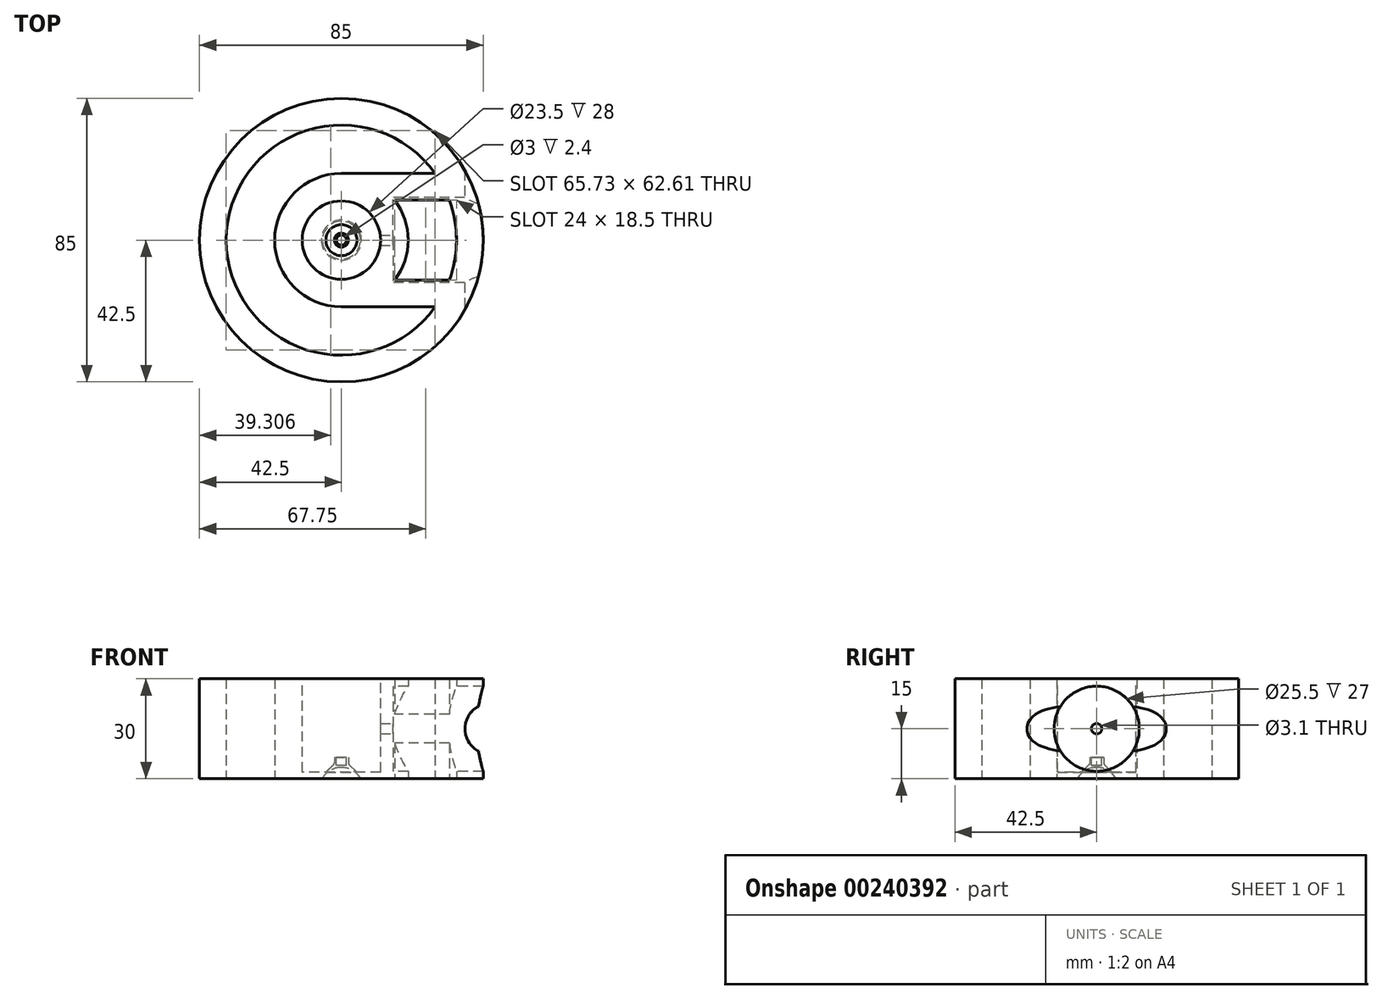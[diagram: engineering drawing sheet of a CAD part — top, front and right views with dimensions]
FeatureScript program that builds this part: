
annotation { "Feature Type Name" : "Feature", "Feature Type Description" : "" }
export const myFeature = defineFeature(function(context is Context, id is Id, definition is map)
    precondition{}
    {
        {
            var Q0;
            Q0=qCreatedBy(makeId("Top.planeOp"),FACE);
            var sketch = newSketch(context, id + "F0", { "sketchPlane" : qUnion([Q0])});
            skCircle(sketch, "E0", {"center": v(0, 0) * mm, "radius": 42.5 * mm});
            skCircle(sketch, "E1", {"center": v(0, 0) * mm, "radius": 34.5 * mm});
            skLineSegment(sketch, "E2.bottom", {"start": v(40.77, -12) * mm, "end": v(15.77, -12) * mm});
            skLineSegment(sketch, "E2.top", {"start": v(40.77, 12) * mm, "end": v(15.77, 12) * mm});
            skLineSegment(sketch, "E2.left", {"start": v(40.77, -12) * mm, "end": v(40.77, 12) * mm});
            skLineSegment(sketch, "E2.right", {"start": v(15.77, -12) * mm, "end": v(15.77, 12) * mm});
            skPoint(sketch, "E2.middle", {"position": v(28.27, 0) * mm});
            skLineSegment(sketch, "E3.0", {"start": v(40.77, -20) * mm, "end": v(7.77, -20) * mm});
            skLineSegment(sketch, "E3.1", {"start": v(7.77, -20) * mm, "end": v(7.77, 20) * mm});
            skLineSegment(sketch, "E3.2", {"start": v(40.77, 20) * mm, "end": v(7.77, 20) * mm});
            skCircle(sketch, "E4", {"center": v(0, 0) * mm, "radius": 20 * mm});
            skLineSegment(sketch, "E5", {"start": v(7.77, 20) * mm, "end": v(0, 20) * mm});
            skLineSegment(sketch, "E6", {"start": v(7.77, -20) * mm, "end": v(0, -20) * mm});
            skSolve(sketch);
        }
        {
            var Q0;
            {var subQ0=sQuery(id+"F0.wireOp",EDGE,"E4");var subQ1=sQuery(id+"F0.wireOp",EDGE,"E3.1");var subQ2=makeQuery(id+"F0.imprint","INTERSECT",VERTEX,{"disambiguationData":[OD(0.0)],"derivedFrom":[subQ1,subQ0]});Q0=makeQuery(id+"F0.imprint","IMPRINT",FACE,{"disambiguationData":[TD([[makeQuery(id+"F0.imprint","IMPRINT",EDGE,{"disambiguationData":[TD([[subQ2,-1.0]])],"derivedFrom":subQ1}),1.0]])]});}
            var Q1;
            {var subQ0=sQuery(id+"F0.wireOp",EDGE,"E5");Q1=makeQuery(id+"F0.imprint","IMPRINT",FACE,{"disambiguationData":[TD([[makeQuery(id+"F0.imprint","IMPRINT",EDGE,{"derivedFrom":subQ0}),1.0]])]});}
            var Q2;
            {var subQ0=sQuery(id+"F0.wireOp",EDGE,"E6");Q2=makeQuery(id+"F0.imprint","IMPRINT",FACE,{"disambiguationData":[TD([[makeQuery(id+"F0.imprint","IMPRINT",EDGE,{"derivedFrom":subQ0}),-1.0]])]});}
            var Q3;
            {var subQ4=sQuery(id+"F0.wireOp",EDGE,"E2.right");Q3=makeQuery(id+"F0.imprint","IMPRINT",FACE,{"disambiguationData":[TD([[makeQuery(id+"F0.imprint","IMPRINT",EDGE,{"derivedFrom":subQ4}),1.0]])]});}
            var Q4;
            {var subQ1=sQuery(id+"F0.wireOp",EDGE,"E3.0");var subQ5=sQuery(id+"F0.wireOp",EDGE,"E1");var subQ6=makeQuery(id+"F0.imprint","INTERSECT",VERTEX,{"derivedFrom":[subQ5,subQ1]});Q4=makeQuery(id+"F0.imprint","IMPRINT",FACE,{"disambiguationData":[TD([[makeQuery(id+"F0.imprint","IMPRINT",EDGE,{"disambiguationData":[TD([[subQ6,-1.0]])],"derivedFrom":subQ5}),1.0]])]});}
            var Q5;
            {var subQ0=sQuery(id+"F0.wireOp",EDGE,"E2.right");Q5=makeQuery(id+"F0.imprint","IMPRINT",FACE,{"disambiguationData":[TD([[makeQuery(id+"F0.imprint","IMPRINT",EDGE,{"derivedFrom":subQ0}),-1.0]])]});}
            var Q6;
            {var subQ1=sQuery(id+"F0.wireOp",EDGE,"E1");var subQ5=sQuery(id+"F0.wireOp",EDGE,"E3.2");var subQ8=makeQuery(id+"F0.imprint","INTERSECT",VERTEX,{"derivedFrom":[subQ1,subQ5]});Q6=makeQuery(id+"F0.imprint","IMPRINT",FACE,{"disambiguationData":[TD([[makeQuery(id+"F0.imprint","IMPRINT",EDGE,{"disambiguationData":[TD([[subQ8,1.0]])],"derivedFrom":subQ1}),1.0]])]});}
            var Q7;
            {var subQ3=sQuery(id+"F0.wireOp",EDGE,"E3.2");var subQ5=sQuery(id+"F0.wireOp",EDGE,"E1");var subQ6=makeQuery(id+"F0.imprint","INTERSECT",VERTEX,{"derivedFrom":[subQ5,subQ3]});Q7=makeQuery(id+"F0.imprint","IMPRINT",FACE,{"disambiguationData":[TD([[makeQuery(id+"F0.imprint","IMPRINT",EDGE,{"disambiguationData":[TD([[subQ6,1.0]])],"derivedFrom":subQ5}),-1.0]])]});}
            var Q8;
            {var subQ0=sQuery(id+"F0.wireOp",EDGE,"E3.2");var subQ1=sQuery(id+"F0.wireOp",EDGE,"E0");var subQ2=makeQuery(id+"F0.imprint","INTERSECT",VERTEX,{"derivedFrom":[subQ1,subQ0]});Q8=makeQuery(id+"F0.imprint","IMPRINT",FACE,{"disambiguationData":[TD([[makeQuery(id+"F0.imprint","IMPRINT",EDGE,{"disambiguationData":[TD([[subQ2,-1.0]])],"derivedFrom":subQ1}),1.0]])]});}
            var Q9;
            {var subQ3=sQuery(id+"F0.wireOp",EDGE,"E3.0");var subQ5=sQuery(id+"F0.wireOp",EDGE,"E1");var subQ6=makeQuery(id+"F0.imprint","INTERSECT",VERTEX,{"derivedFrom":[subQ5,subQ3]});Q9=makeQuery(id+"F0.imprint","IMPRINT",FACE,{"disambiguationData":[TD([[makeQuery(id+"F0.imprint","IMPRINT",EDGE,{"disambiguationData":[TD([[subQ6,-1.0]])],"derivedFrom":subQ5}),-1.0]])]});}
            var Q10;
            {var subQ5=sQuery(id+"F0.wireOp",EDGE,"E2.left");Q10=makeQuery(id+"F0.imprint","IMPRINT",FACE,{"disambiguationData":[TD([[makeQuery(id+"F0.imprint","IMPRINT",EDGE,{"derivedFrom":subQ5}),1.0]])]});}
            var Q11;
            {var subQ0=sQuery(id+"F0.wireOp",EDGE,"E2.left");Q11=makeQuery(id+"F0.imprint","IMPRINT",FACE,{"disambiguationData":[TD([[makeQuery(id+"F0.imprint","IMPRINT",EDGE,{"derivedFrom":subQ0}),-1.0]])]});}
            extrude(context, id + "F1", {"entities" : qUnion([Q0, Q1, Q2, Q3, Q4, Q5, Q6, Q7, Q8, Q9, Q10, Q11]), "depth" : 30 * mm});
        }
        {
            var Q0;
            Q0=qCreatedBy(makeId("Right.planeOp"),FACE);
            var sketch = newSketch(context, id + "F2", { "sketchPlane" : qUnion([Q0])});
            skCircle(sketch, "E7", {"center": v(0, 15) * mm, "radius": 12.75 * mm});
            skSolve(sketch);
        }
        {
            var Q0;
            Q0 = qSketchRegion(id + "F2", true);
            extrude(context, id + "F3", {"entities" : qUnion([Q0]), "operationType" : NewBodyOperationType.REMOVE, "depth" : (15.5 + 30) * mm, "hasSecondDirection" : true, "secondDirectionOppositeDirection" : false, "secondDirectionDepth" : 15.5 * mm});
        }
        {
            var Q0;
            Q0=qCreatedBy(makeId("Front.planeOp"),FACE);
            var sketch = newSketch(context, id + "F4", { "sketchPlane" : qUnion([Q0])});
            skCircle(sketch, "E8", {"center": v(44.5, 15) * mm, "radius": 7.5 * mm});
            skSolve(sketch);
        }
        {
            var Q0;
            Q0 = qSketchRegion(id + "F4", true);
            extrude(context, id + "F5", {"entities" : qUnion([Q0]), "operationType" : NewBodyOperationType.REMOVE, "oppositeDirection" : true, "depth" : 25 * mm, "hasSecondDirection" : true, "secondDirectionOppositeDirection" : false, "secondDirectionDepth" : 25 * mm});
        }
        {
            var Q0;
            Q0=makeQuery(id+"F1.opExtrude","CAP_FACE",FACE,{"disambiguationData":[OSD([sQuery(id+"F0.wireOp",EDGE,"E0"),sQuery(id+"F0.wireOp",EDGE,"E1"),sQuery(id+"F0.wireOp",EDGE,"E2.bottom"),sQuery(id+"F0.wireOp",EDGE,"E2.top"),sQuery(id+"F0.wireOp",EDGE,"E3.0"),sQuery(id+"F0.wireOp",EDGE,"E3.2"),sQuery(id+"F0.wireOp",EDGE,"E4"),sQuery(id+"F0.wireOp",EDGE,"E5"),sQuery(id+"F0.wireOp",EDGE,"E6")])],"isStart":false});
            var sketch = newSketch(context, id + "F6", { "sketchPlane" : qUnion([Q0])});
            skCircle(sketch, "E9", {"center": v(0, 0) * mm, "radius": 11.75 * mm});
            skSolve(sketch);
        }
        {
            var Q0;
            Q0 = qSketchRegion(id + "F6", true);
            extrude(context, id + "F7", {"entities" : qUnion([Q0]), "operationType" : NewBodyOperationType.REMOVE, "oppositeDirection" : true, "depth" : 28 * mm});
        }
        {
            var Q0;
            Q0=makeQuery(id+"F3.boolean.opBoolean","COPY",FACE,{"derivedFrom":makeQuery(id+"F3.opExtrude","CAP_FACE",FACE,{"disambiguationData":[OSD([sQuery(id+"F2.wireOp",EDGE,"E7")])],"isStart":true})});
            var sketch = newSketch(context, id + "F8", { "sketchPlane" : qUnion([Q0])});
            skCircle(sketch, "E10", {"center": v(0, 15) * mm, "radius": 1.55 * mm});
            skSolve(sketch);
        }
        {
            var Q0;
            Q0 = qSketchRegion(id + "F8", true);
            extrude(context, id + "F9", {"entities" : qUnion([Q0]), "operationType" : NewBodyOperationType.REMOVE, "oppositeDirection" : true, "depth" : 10 * mm});
        }
        {
            var Q0;
            Q0=qCreatedBy(makeId("Front.planeOp"),FACE);
            var sketch = newSketch(context, id + "F10", { "sketchPlane" : qUnion([Q0])});
            skLineSegment(sketch, "E11", {"start": v(-4.65, 2) * mm, "end": v(-2.1, 4.4) * mm});
            skLineSegment(sketch, "E12", {"start": v(-2.1, 4.4) * mm, "end": v(2.1, 4.4) * mm});
            skLineSegment(sketch, "E13", {"start": v(2.1, 4.4) * mm, "end": v(4.65, 2) * mm});
            skLineSegment(sketch, "E14", {"start": v(4.65, 2) * mm, "end": v(-4.65, 2) * mm});
            skLineSegment(sketch, "E15", {"start": v(0, 0) * mm, "end": v(0, 13.24) * mm, "construction": true});
            skLineSegment(sketch, "E16", {"start": v(0, 4.4) * mm, "end": v(0, 2) * mm});
            skSolve(sketch);
        }
        {
            var Q0;
            {var subQ0=sQuery(id+"F10.wireOp",EDGE,"E13");Q0=makeQuery(id+"F10.imprint","IMPRINT",FACE,{"disambiguationData":[TD([[makeQuery(id+"F10.imprint","IMPRINT",EDGE,{"derivedFrom":subQ0}),-1.0]])]});}
            var Q1;
            Q1=sQuery(id+"F10.wireOp",EDGE,"E15");
            revolve(context, id + "F11", {"operationType" : NewBodyOperationType.ADD, "entities" : qUnion([Q0]), "axis" : qUnion([Q1]), "revolveType" : RevolveType.FULL});
        }
        {
            var Q0;
            Q0=qCreatedBy(makeId("Front.planeOp"),FACE);
            var sketch = newSketch(context, id + "F12", { "sketchPlane" : qUnion([Q0])});
            skCircle(sketch, "E17", {"center": v(0, -3.25) * mm, "radius": 6.65 * mm});
            skLineSegment(sketch, "E18", {"start": v(0, 3.4) * mm, "end": v(0, -9.9) * mm});
            skSolve(sketch);
        }
        {
            var Q0;
            {var subQ0=sQuery(id+"F12.wireOp",EDGE,"E18");Q0=makeQuery(id+"F12.imprint","IMPRINT",FACE,{"disambiguationData":[TD([[makeQuery(id+"F12.imprint","IMPRINT",EDGE,{"derivedFrom":subQ0}),1.0]])]});}
            var Q1;
            Q1=sQuery(id+"F12.wireOp",EDGE,"E18");
            revolve(context, id + "F13", {"operationType" : NewBodyOperationType.REMOVE, "entities" : qUnion([Q0]), "axis" : qUnion([Q1]), "revolveType" : RevolveType.FULL, "oppositeDirection" : true});
        }
        {
            var Q0;
            Q0=makeQuery(id+"F11.opRevolve","SWEPT_FACE",FACE,{"disambiguationData":[OSD([sQuery(id+"F10.wireOp",EDGE,"E12")])]});
            var sketch = newSketch(context, id + "F14", { "sketchPlane" : qUnion([Q0])});
            skSolve(sketch);
        }
        {
            var Q0;
            Q0 = qSketchRegion(id + "F14", true);
            var Q1;
            Q1=makeQuery(id+"F14.imprint","IMPRINT",FACE,{"disambiguationData":[TD([[makeQuery(id+"F14.imprint","IMPRINT",EDGE,{"derivedFrom":makeQuery(id+"F11.opRevolve","SWEPT_EDGE",EDGE,{"disambiguationData":[OSD([sQuery(id+"F10.wireOp",EDGE,"E12"),sQuery(id+"F10.wireOp",EDGE,"E13")])]})}),-1.0]])]});
            extrude(context, id + "F15", {"entities" : qUnion([Q0, Q1]), "operationType" : NewBodyOperationType.ADD, "depth" : 2 * mm});
        }
        {
            var Q0;
            Q0=makeQuery(id+"F15.opExtrude","CAP_FACE",FACE,{"disambiguationData":[OSD([sQuery(id+"F10.wireOp",EDGE,"E12"),sQuery(id+"F10.wireOp",EDGE,"E13")])],"isStart":false});
            var sketch = newSketch(context, id + "F16", { "sketchPlane" : qUnion([Q0])});
            skCircle(sketch, "E19", {"center": v(0, 0) * mm, "radius": 1.5 * mm});
            skSolve(sketch);
        }
        {
            var Q0;
            Q0 = qSketchRegion(id + "F16", true);
            extrude(context, id + "F17", {"entities" : qUnion([Q0]), "operationType" : NewBodyOperationType.REMOVE, "oppositeDirection" : true, "depth" : 2.4 * mm});
        }
        {
            var Q0;
            {var subQ0=sQuery(id+"F10.wireOp",EDGE,"E13");var subQ1=sQuery(id+"F10.wireOp",EDGE,"E12");Q0=makeQuery(id+"F15.boolean.opBoolean","MERGE",EDGE,{"derivedFrom":[makeQuery(id+"F11.opRevolve","SWEPT_EDGE",EDGE,{"disambiguationData":[OSD([subQ1,subQ0])]}),makeQuery(id+"F15.opExtrude","CAP_EDGE",EDGE,{"disambiguationData":[OSD([subQ1,subQ0])],"isStart":true})]});}
            var Q1;
            Q1=makeQuery(id+"F11.opRevolve","SWEPT_EDGE",EDGE,{"disambiguationData":[OSD([sQuery(id+"F10.wireOp",EDGE,"E13"),sQuery(id+"F10.wireOp",EDGE,"E14")])]});
            fillet(context, id + "F18", {"entities" : qUnion([Q0, Q1]), "radius" : 1 * mm, "tangentPropagation" : true, "allowEdgeOverflow" : false});
        }
        {
            var Q0;
            Q0=makeQuery(id+"F13.boolean.opBoolean","INTERSECT",EDGE,{"derivedFrom":[makeQuery(id+"F1.opExtrude","CAP_FACE",FACE,{"disambiguationData":[OSD([sQuery(id+"F0.wireOp",EDGE,"E0"),sQuery(id+"F0.wireOp",EDGE,"E1"),sQuery(id+"F0.wireOp",EDGE,"E2.bottom"),sQuery(id+"F0.wireOp",EDGE,"E2.top"),sQuery(id+"F0.wireOp",EDGE,"E3.0"),sQuery(id+"F0.wireOp",EDGE,"E3.2"),sQuery(id+"F0.wireOp",EDGE,"E4"),sQuery(id+"F0.wireOp",EDGE,"E5"),sQuery(id+"F0.wireOp",EDGE,"E6")])],"isStart":true}),makeQuery(id+"F13.opRevolve","SWEPT_FACE",FACE,{"disambiguationData":[OSD([sQuery(id+"F12.wireOp",EDGE,"E17")])]})]});
            chamfer(context, id + "F19", {"entities" : qUnion([Q0]), "width" : 0.4 * mm, "tangentPropagation" : true});
        }
    });
